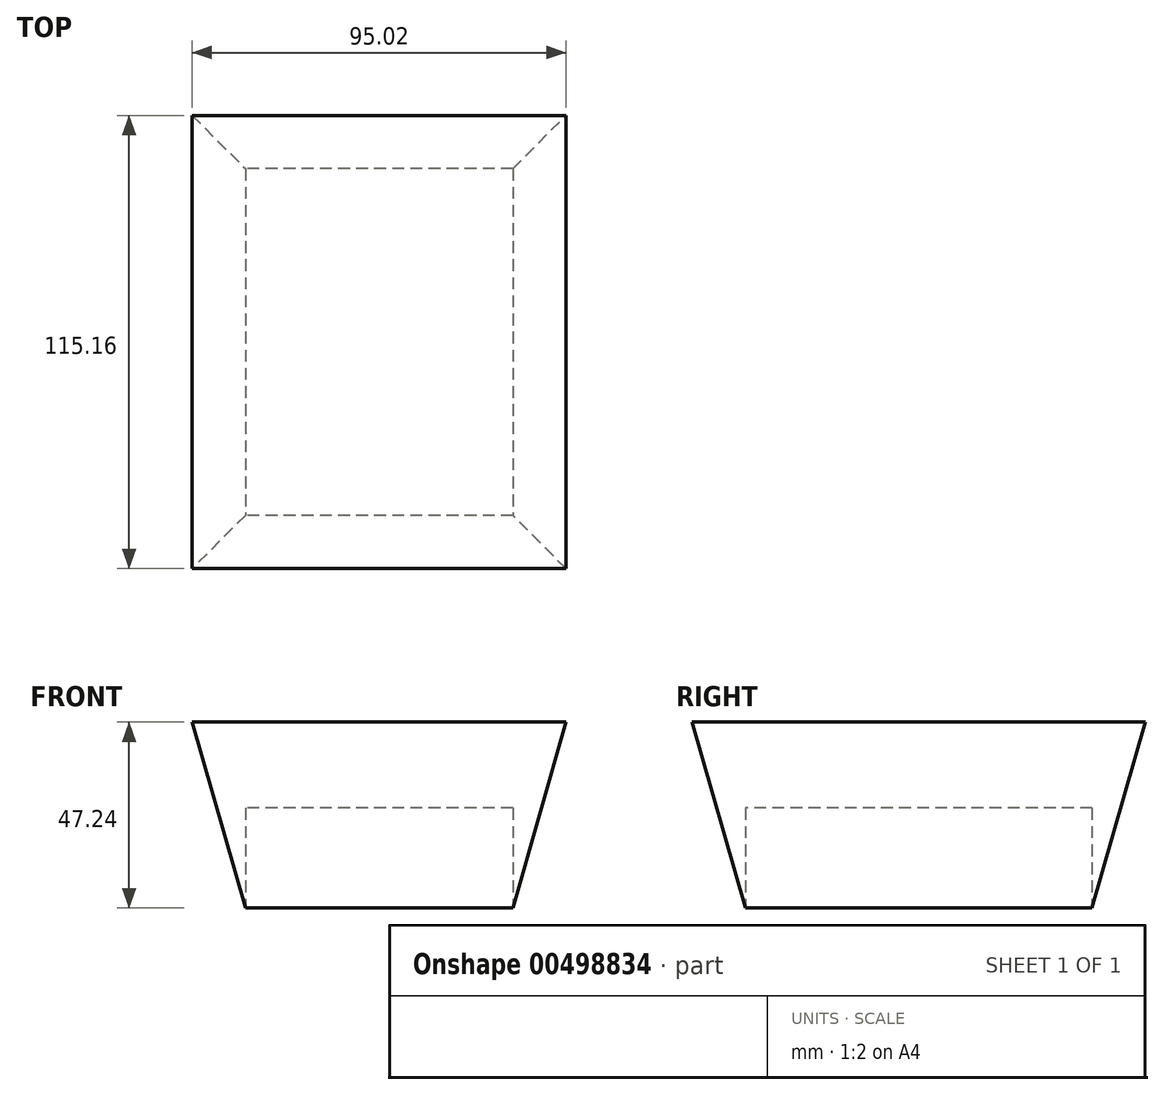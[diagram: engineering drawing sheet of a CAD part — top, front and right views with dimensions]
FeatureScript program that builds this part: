
annotation { "Feature Type Name" : "Feature", "Feature Type Description" : "" }
export const myFeature = defineFeature(function(context is Context, id is Id, definition is map)
    precondition{}
    {
        {
            var Q0;
            Q0=qCreatedBy(makeId("Top.planeOp"),FACE);
            var sketch = newSketch(context, id + "F0", { "sketchPlane" : qUnion([Q0])});
            skLineSegment(sketch, "E0.bottom", {"start": v(33.96, 44.03) * mm, "end": v(-33.96, 44.03) * mm});
            skLineSegment(sketch, "E0.top", {"start": v(33.96, -44.03) * mm, "end": v(-33.96, -44.03) * mm});
            skLineSegment(sketch, "E0.left", {"start": v(33.96, 44.03) * mm, "end": v(33.96, -44.03) * mm});
            skLineSegment(sketch, "E0.right", {"start": v(-33.96, 44.03) * mm, "end": v(-33.96, -44.03) * mm});
            skPoint(sketch, "E0.middle", {"position": v(0, 0) * mm});
            skSolve(sketch);
        }
        {
            var Q0;
            Q0=makeQuery(id+"F0.imprint","IMPRINT",FACE,{"disambiguationData":[TD([[makeQuery(id+"F0.imprint","IMPRINT",EDGE,{"derivedFrom":sQuery(id+"F0.wireOp",EDGE,"E0.bottom")}),1.0]])]});
            extrude(context, id + "F1", {"entities" : qUnion([Q0]), "depth" : 47.24 * mm, "hasDraft" : true, "draftAngle" : 16 * degree});
        }
        {
            var Q0;
            Q0=makeQuery(id+"F0.imprint","IMPRINT",FACE,{"disambiguationData":[TD([[makeQuery(id+"F0.imprint","IMPRINT",EDGE,{"derivedFrom":sQuery(id+"F0.wireOp",EDGE,"E0.bottom")}),1.0]])]});
            extrude(context, id + "F2", {"entities" : qUnion([Q0]), "depth" : 25.4 * mm});
        }
    });
